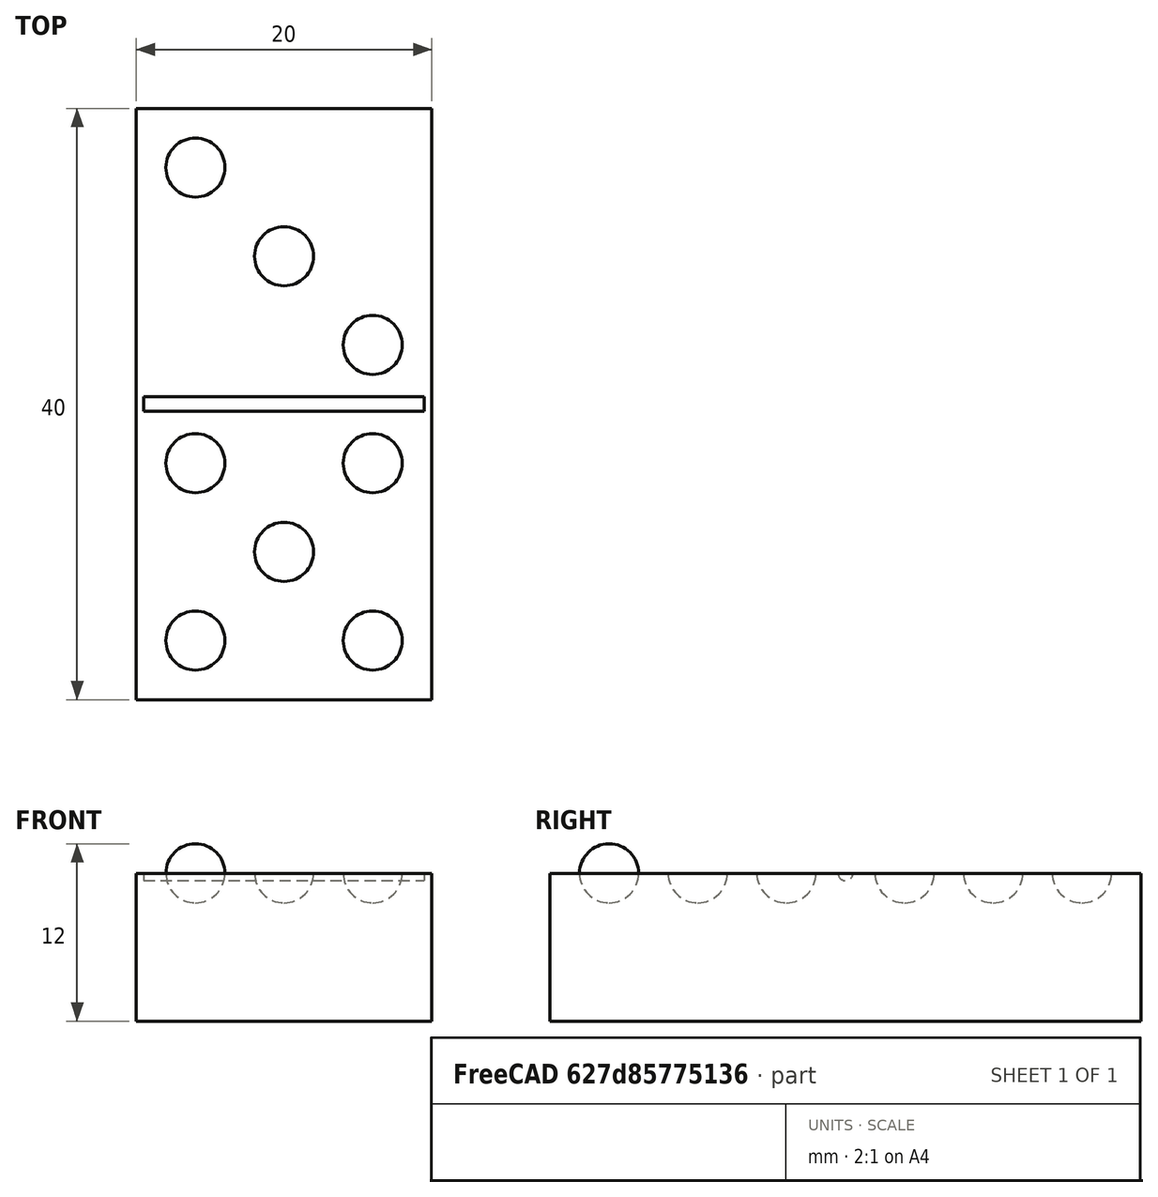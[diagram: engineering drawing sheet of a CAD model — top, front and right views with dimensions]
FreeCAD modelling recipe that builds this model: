
FCSTD DOCUMENT  (FreeCAD 0.21R33694 (Git))
Label: OJT1_T013_domino
License: All rights reserved
LicenseURL: https://en.wikipedia.org/wiki/All_rights_reserved
objects: Part::Cut×6, Part::Sphere×4, Part::FeaturePython×2, Part::Box×1, Part::Cylinder×1
note: 12 computed .brp shape members not serialized (recipe doc carries the construction recipe); baked Part::Feature solids carry a one-line shape summary decoded from their .brp

FEATURE [Part::Box] Box  label="Cub"
  AttacherType = Attacher::AttachEngine3D
  Height = 10
  Length = 20
  Width = 40
FEATURE [Part::Cylinder] Cylinder  label="Cilindre"
  Angle = 360
  AttacherType = Attacher::AttachEngine3D
  FirstAngle = 0
  Height = 19
  Placement = pos=(19.5,20,10) rot=(0,-1,0;1.5708rad)
  Radius = 0.5
  SecondAngle = 0
  expr: .Placement.Base.x = 19.5
  expr: .Placement.Base.y = 20
  expr: .Placement.Rotation.Pitch = -90
  expr: .Placement.Rotation.Roll = 0
  expr: .Placement.Rotation.Yaw = 0
FEATURE [Part::Cut] Cut
  Base = -> Box
  Tool = -> Cylinder
FEATURE [Part::Sphere] Sphere  label="Esfera"
  Angle1 = -90
  Angle2 = 90
  Angle3 = 360
  AttacherType = Attacher::AttachEngine3D
  Placement = pos=(4,4,10) rot=(0,0,1;0rad)
  Radius = 2
FEATURE [Part::FeaturePython] Array  # Draft array (typed FeaturePython)
  AlwaysSyncPlacement = false
  Angle = 360
  ArrayType = 0
  Axis = (0,0,1)
  Base = -> Sphere
  Center = (0,0,0)
  Count = 4
  ExpandArray = false
  Fuse = false
  IntervalAxis = (0,0,0)
  IntervalX = (12,0,0)
  IntervalY = (0,12,0)
  IntervalZ = (0,0,100)
  NumberCircles = 3
  NumberPolar = 5
  NumberX = 2
  NumberY = 2
  NumberZ = 1
  PlacementList = 4 placements: [(4,4,10),(4,16,10),(16,4,10),(16,16,10)]
  RadialDistance = 50
  ScaleList = (4) [(1,1,1),(1,1,1),(1,1,1),(1,1,1)]
  Symmetry = 1
  TangentialDistance = 25
FEATURE [Part::Cut] Cut001
  Base = -> Cut
  Tool = -> Array
FEATURE [Part::Sphere] Sphere001  label="Esfera001"
  Angle1 = -90
  Angle2 = 90
  Angle3 = 360
  AttacherType = Attacher::AttachEngine3D
  Placement = pos=(10,10,10) rot=(0,0,1;0rad)
  Radius = 2
FEATURE [Part::Cut] Cut002
  Base = -> Cut001
  Tool = -> Sphere001
FEATURE [Part::FeaturePython] Array001  # Draft array (typed FeaturePython)
  AlwaysSyncPlacement = false
  Angle = 360
  ArrayType = 0
  Axis = (0,0,1)
  Base = -> Sphere001
  Center = (0,0,0)
  Count = 4
  ExpandArray = false
  Fuse = false
  IntervalAxis = (0,0,0)
  IntervalX = (0,0,0)
  IntervalY = (0,20,0)
  IntervalZ = (0,0,100)
  NumberCircles = 3
  NumberPolar = 5
  NumberX = 2
  NumberY = 2
  NumberZ = 1
  PlacementList = 4 placements: [(10,10,10),(10,30,10),(10,10,10),(10,30,10)]
  RadialDistance = 50
  ScaleList = (4) [(1,1,1),(1,1,1),(1,1,1),(1,1,1)]
  Symmetry = 1
  TangentialDistance = 25
FEATURE [Part::Cut] Cut003
  Base = -> Cut002
  Tool = -> Array001
FEATURE [Part::Sphere] Sphere002  label="Esfera002"
  Angle1 = -90
  Angle2 = 90
  Angle3 = 360
  AttacherType = Attacher::AttachEngine3D
  Placement = pos=(16,24,10) rot=(0,0,1;0rad)
  Radius = 2
FEATURE [Part::Cut] Cut004
  Base = -> Cut003
  Tool = -> Sphere002
FEATURE [Part::Sphere] Sphere003  label="Esfera003"
  Angle1 = -90
  Angle2 = 90
  Angle3 = 360
  AttacherType = Attacher::AttachEngine3D
  Placement = pos=(4,36,10) rot=(0,0,1;0rad)
  Radius = 2
FEATURE [Part::Cut] Cut005
  Base = -> Cut004
  Tool = -> Sphere003
